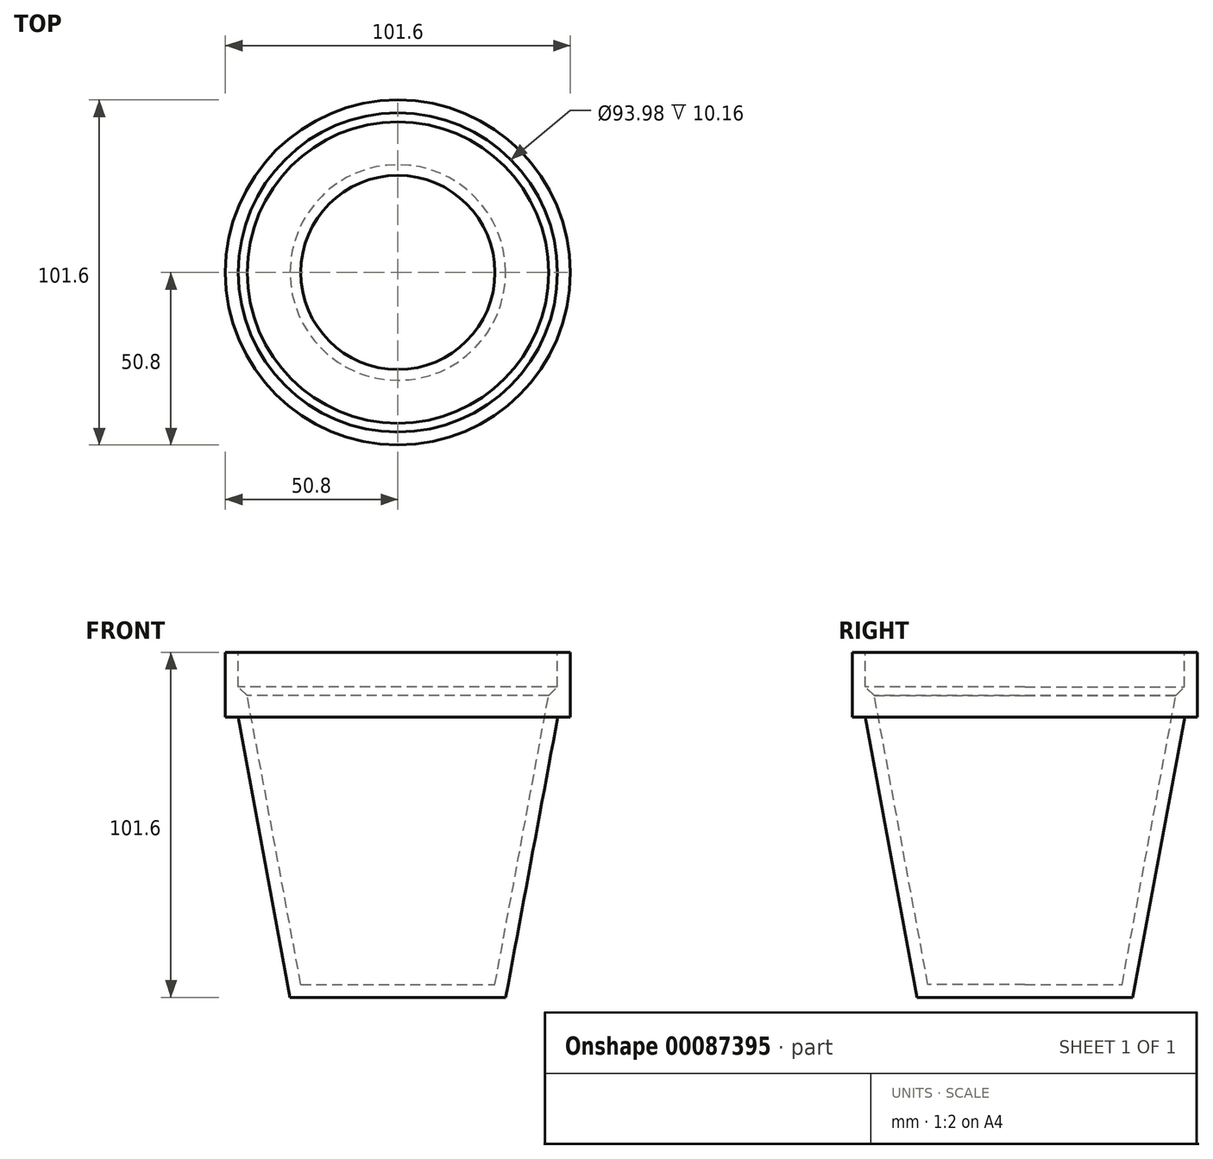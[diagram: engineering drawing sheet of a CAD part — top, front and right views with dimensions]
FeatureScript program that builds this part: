
annotation { "Feature Type Name" : "Feature", "Feature Type Description" : "" }
export const myFeature = defineFeature(function(context is Context, id is Id, definition is map)
    precondition{}
    {
        {
            var Q0;
            Q0=qCreatedBy(makeId("Front.planeOp"),FACE);
            var sketch = newSketch(context, id + "F0", { "sketchPlane" : qUnion([Q0])});
            skLineSegment(sketch, "E0", {"start": v(0, 132.66) * mm, "end": v(0, -118.93) * mm, "construction": true});
            skLineSegment(sketch, "E1", {"start": v(0, 56.4) * mm, "end": v(-50.8, 56.4) * mm});
            skLineSegment(sketch, "E2", {"start": v(-50.8, 56.4) * mm, "end": v(-50.8, 37.35) * mm});
            skLineSegment(sketch, "E3", {"start": v(-50.8, 37.35) * mm, "end": v(-47.08, 37.35) * mm});
            skLineSegment(sketch, "E4", {"start": v(-47.08, 37.35) * mm, "end": v(-31.75, -45.2) * mm});
            skLineSegment(sketch, "E5", {"start": v(-31.75, -45.2) * mm, "end": v(0, -45.2) * mm});
            skLineSegment(sketch, "E6", {"start": v(0, -45.2) * mm, "end": v(0, 56.4) * mm});
            skSolve(sketch);
        }
        {
            var Q0;
            Q0 = qSketchRegion(id + "F0", true);
            var Q1;
            Q1=sQuery(id+"F0.wireOp",EDGE,"E0");
            revolve(context, id + "F1", {"entities" : qUnion([Q0]), "axis" : qUnion([Q1]), "revolveType" : RevolveType.FULL});
        }
        {
            var Q0;
            Q0=makeQuery(id+"F1.opRevolve","SWEPT_FACE",FACE,{"disambiguationData":[OSD([sQuery(id+"F0.wireOp",EDGE,"E1")])]});
            shell(context, id + "F2", {"entities" : qUnion([Q0]), "thickness" : 3.8 * mm});
        }
        {
            var Q0;
            Q0=makeQuery(id+"F2.opShell","OFFSET_EDGE",EDGE,{"disambiguationData":[OSD([sQuery(id+"F0.wireOp",EDGE,"E2"),sQuery(id+"F0.wireOp",EDGE,"E3")])]});
            chamfer(context, id + "F3", {"entities" : qUnion([Q0]), "width" : 5.08 * mm, "tangentPropagation" : true});
        }
    });
